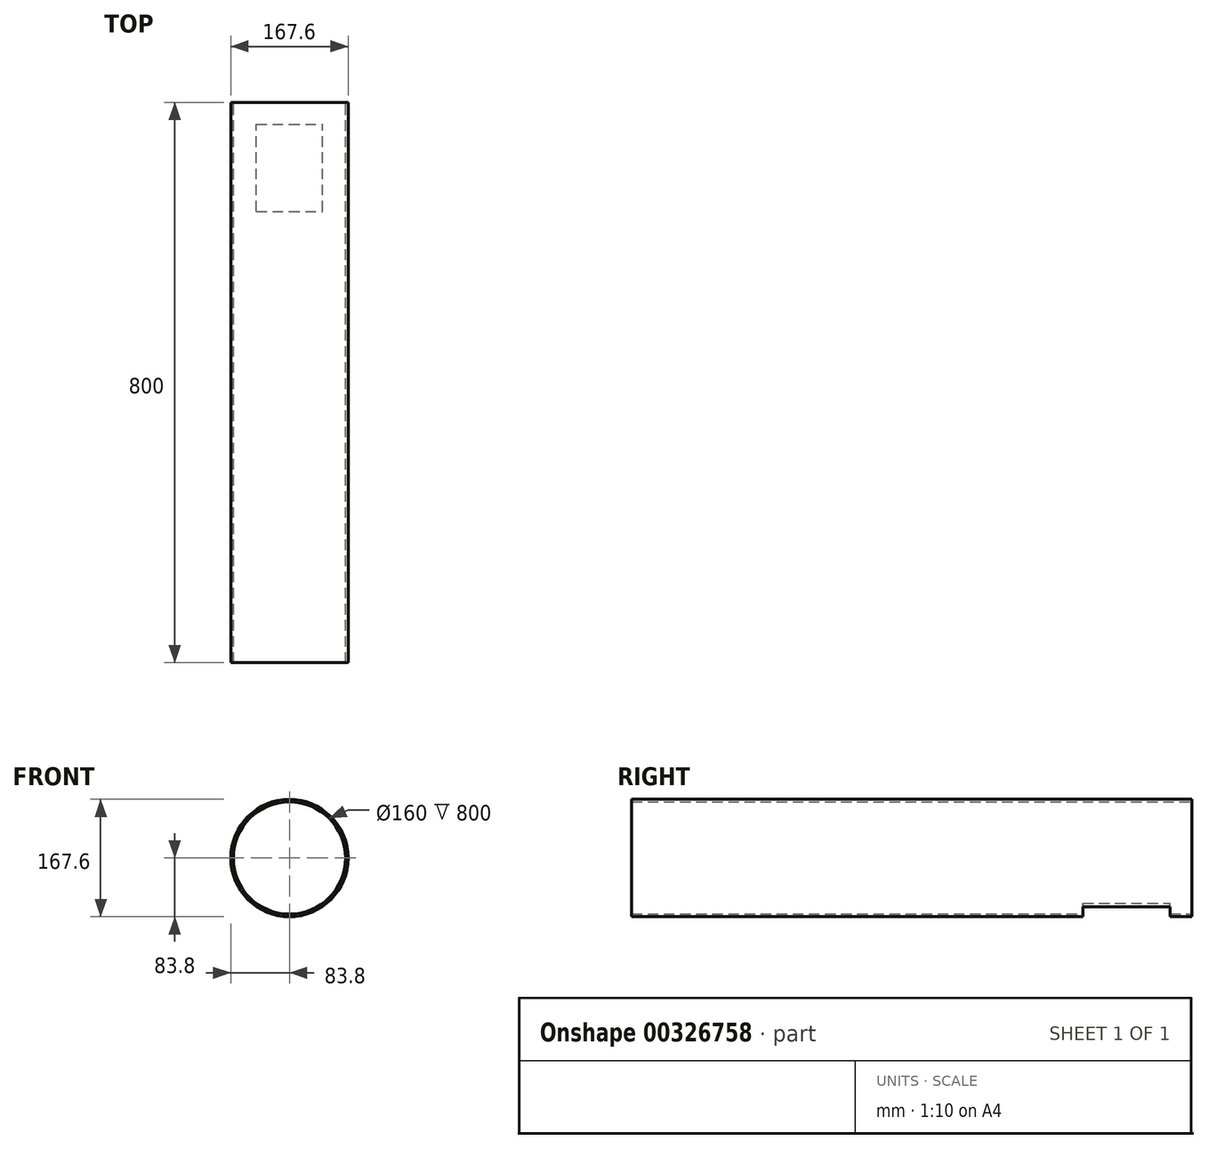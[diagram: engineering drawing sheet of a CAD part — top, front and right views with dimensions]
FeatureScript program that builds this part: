
annotation { "Feature Type Name" : "Feature", "Feature Type Description" : "" }
export const myFeature = defineFeature(function(context is Context, id is Id, definition is map)
    precondition{}
    {
        {
            var Q0;
            Q0=qCreatedBy(makeId("Front.planeOp"),FACE);
            var sketch = newSketch(context, id + "F0", { "sketchPlane" : qUnion([Q0])});
            skCircle(sketch, "E0", {"center": v(0, 0) * mm, "radius": 80 * mm});
            skCircle(sketch, "E1.0", {"center": v(0, 0) * mm, "radius": 83.8 * mm});
            skSolve(sketch);
        }
        {
            var Q0;
            Q0 = qSketchRegion(id + "F0", true);
            extrude(context, id + "F1", {"entities" : qUnion([Q0]), "depth" : 800 * mm});
        }
        {
            var Q0;
            Q0=qCreatedBy(makeId("Top.planeOp"),FACE);
            var sketch = newSketch(context, id + "F2", { "sketchPlane" : qUnion([Q0])});
            skLineSegment(sketch, "E2.bottom", {"start": v(-47.16, -31.13) * mm, "end": v(47.16, -31.13) * mm});
            skLineSegment(sketch, "E2.top", {"start": v(-47.16, -155.63) * mm, "end": v(47.16, -155.63) * mm});
            skLineSegment(sketch, "E2.left", {"start": v(-47.16, -31.13) * mm, "end": v(-47.16, -155.63) * mm});
            skLineSegment(sketch, "E2.right", {"start": v(47.16, -31.13) * mm, "end": v(47.16, -155.63) * mm});
            skPoint(sketch, "E2.middle", {"position": v(0, -93.38) * mm});
            skSolve(sketch);
        }
        {
            var Q0;
            Q0 = qSketchRegion(id + "F2", true);
            var Q1;
            Q1=makeQuery(id+"F1.opExtrude","SWEPT_FACE",FACE,{"disambiguationData":[OSD([sQuery(id+"F0.wireOp",EDGE,"E1.0")])]});
            extrude(context, id + "F3", {"entities" : qUnion([Q0]), "operationType" : NewBodyOperationType.REMOVE, "endBound" : BoundingType.UP_TO_SURFACE, "oppositeDirection" : true, "endBoundEntityFace" : qUnion([Q1]), "depth" : 25 * mm});
        }
    });
